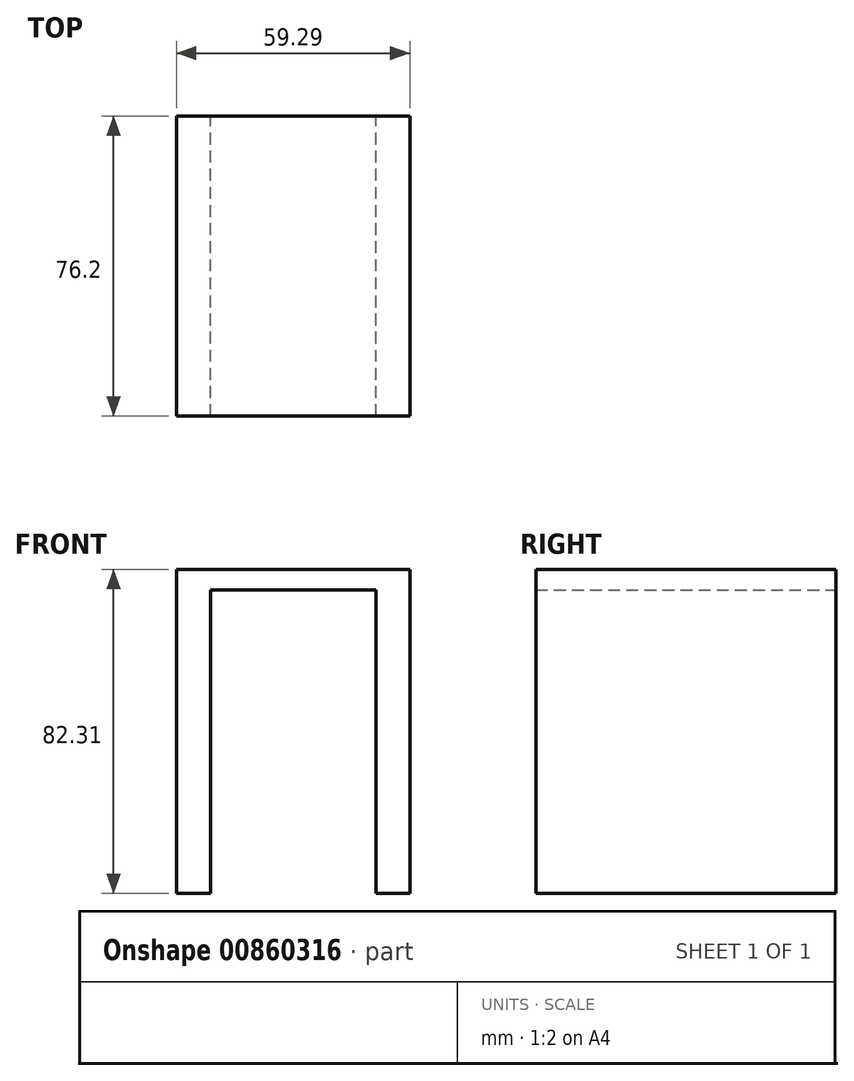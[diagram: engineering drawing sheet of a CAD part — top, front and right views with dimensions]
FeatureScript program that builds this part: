
annotation { "Feature Type Name" : "Feature", "Feature Type Description" : "" }
export const myFeature = defineFeature(function(context is Context, id is Id, definition is map)
    precondition{}
    {
        {
            var Q0;
            Q0=qCreatedBy(makeId("Front.planeOp"),FACE);
            var sketch = newSketch(context, id + "F0", { "sketchPlane" : qUnion([Q0])});
            skLineSegment(sketch, "E0", {"start": v(-47.92, -47.34) * mm, "end": v(-47.92, 29.79) * mm});
            skLineSegment(sketch, "E1", {"start": v(-47.92, -47.34) * mm, "end": v(-39.29, -47.34) * mm});
            skLineSegment(sketch, "E2", {"start": v(-39.29, -47.34) * mm, "end": v(-39.29, 29.79) * mm});
            skLineSegment(sketch, "E3", {"start": v(-47.92, 29.79) * mm, "end": v(-39.29, 29.79) * mm});
            skLineSegment(sketch, "E4", {"start": v(2.73, -47.34) * mm, "end": v(2.73, 29.79) * mm});
            skLineSegment(sketch, "E5", {"start": v(2.73, 29.79) * mm, "end": v(11.37, 29.79) * mm});
            skLineSegment(sketch, "E6", {"start": v(11.37, 29.79) * mm, "end": v(11.37, -47.34) * mm});
            skLineSegment(sketch, "E7", {"start": v(2.73, -47.34) * mm, "end": v(11.37, -47.34) * mm});
            skLineSegment(sketch, "E8", {"start": v(-39.29, 29.79) * mm, "end": v(7.05, 29.79) * mm});
            skLineSegment(sketch, "E9", {"start": v(11.37, 29.79) * mm, "end": v(11.37, 34.97) * mm});
            skLineSegment(sketch, "E10", {"start": v(11.37, 34.97) * mm, "end": v(-47.92, 34.97) * mm});
            skLineSegment(sketch, "E11", {"start": v(-47.92, 29.79) * mm, "end": v(-47.92, 34.97) * mm});
            skSolve(sketch);
        }
        {
            var Q0;
            {var subQ1=sQuery(id+"F0.wireOp",EDGE,"E4");Q0=makeQuery(id+"F0.imprint","IMPRINT",FACE,{"disambiguationData":[TD([[makeQuery(id+"F0.imprint","IMPRINT",EDGE,{"derivedFrom":subQ1}),-1.0]])]});}
            var Q1;
            {var subQ3=sQuery(id+"F0.wireOp",EDGE,"E3");Q1=makeQuery(id+"F0.imprint","IMPRINT",FACE,{"disambiguationData":[TD([[makeQuery(id+"F0.imprint","IMPRINT",EDGE,{"derivedFrom":subQ3}),1.0]])]});}
            var Q2;
            Q2=makeQuery(id+"F0.imprint","IMPRINT",FACE,{"disambiguationData":[TD([[makeQuery(id+"F0.imprint","IMPRINT",EDGE,{"derivedFrom":sQuery(id+"F0.wireOp",EDGE,"E0")}),-1.0]])]});
            extrude(context, id + "F1", {"entities" : qUnion([Q0, Q1, Q2]), "depth" : 76.2 * mm, "offsetDistance" : 25.4 * mm});
        }
    });
